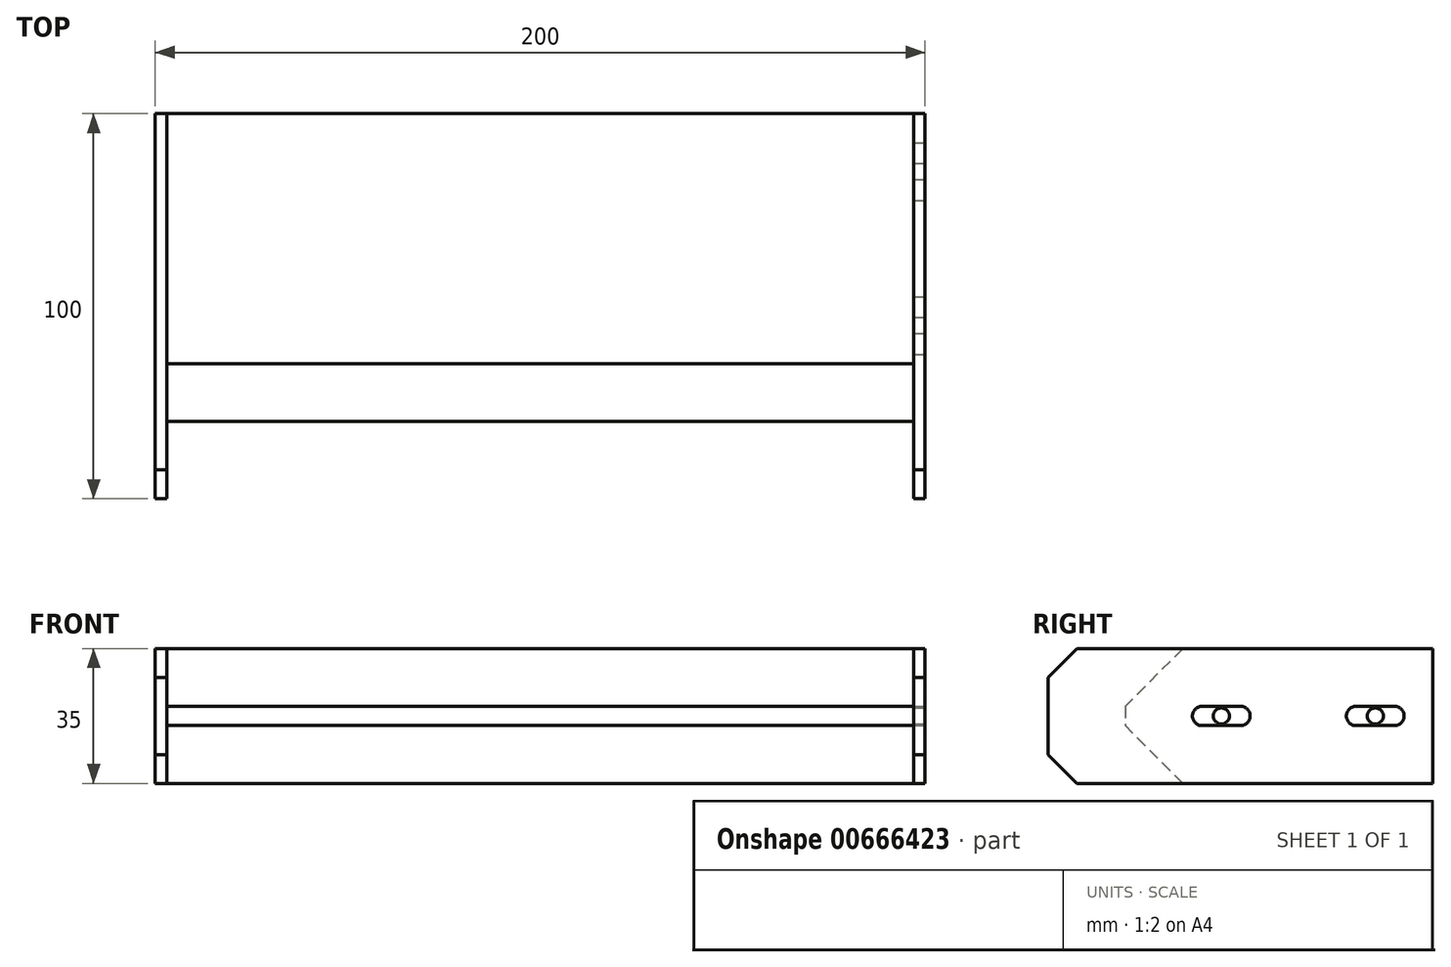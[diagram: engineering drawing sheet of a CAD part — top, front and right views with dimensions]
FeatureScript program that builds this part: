
annotation { "Feature Type Name" : "Feature", "Feature Type Description" : "" }
export const myFeature = defineFeature(function(context is Context, id is Id, definition is map)
    precondition{}
    {
        {
            var Q0;
            Q0=qCreatedBy(makeId("Top.planeOp"),FACE);
            var sketch = newSketch(context, id + "F0", { "sketchPlane" : qUnion([Q0])});
            skLineSegment(sketch, "E0.bottom", {"start": v(100, 50) * mm, "end": v(-100, 50) * mm});
            skLineSegment(sketch, "E0.top", {"start": v(100, -50) * mm, "end": v(97, -50) * mm});
            skLineSegment(sketch, "E0.left", {"start": v(100, 50) * mm, "end": v(100, -50) * mm});
            skLineSegment(sketch, "E0.right", {"start": v(-100, 50) * mm, "end": v(-100, -50) * mm});
            skPoint(sketch, "E0.middle", {"position": v(0, 0) * mm});
            skLineSegment(sketch, "E1", {"start": v(-97, -50) * mm, "end": v(-97, -30) * mm});
            skLineSegment(sketch, "E2", {"start": v(-97, -30) * mm, "end": v(97, -30) * mm});
            skLineSegment(sketch, "E3", {"start": v(97, -30) * mm, "end": v(97, -50) * mm});
            skLineSegment(sketch, "E4.trimOffspring", {"start": v(-97, -50) * mm, "end": v(-100, -50) * mm});
            skSolve(sketch);
        }
        {
            var Q0;
            Q0 = qSketchRegion(id + "F0", true);
            extrude(context, id + "F1", {"entities" : qUnion([Q0]), "depth" : 17.5 * mm, "offsetDistance" : 25 * mm, "hasSecondDirection" : true, "secondDirectionOppositeDirection" : true, "secondDirectionDepth" : 17.5 * mm});
        }
        {
            var Q0;
            Q0=makeQuery(id+"F1.opExtrude","CAP_EDGE",EDGE,{"disambiguationData":[OSD([sQuery(id+"F0.wireOp",EDGE,"E2")])],"isStart":false});
            var Q1;
            Q1=makeQuery(id+"F1.opExtrude","CAP_EDGE",EDGE,{"disambiguationData":[OSD([sQuery(id+"F0.wireOp",EDGE,"E2")])],"isStart":true});
            chamfer(context, id + "F2", {"entities" : qUnion([Q0, Q1]), "width" : 15 * mm, "tangentPropagation" : true});
        }
        {
            var Q0;
            Q0=makeQuery(id+"F1.opExtrude","CAP_EDGE",EDGE,{"disambiguationData":[OSD([sQuery(id+"F0.wireOp",EDGE,"E0.top")])],"isStart":false});
            var Q1;
            Q1=makeQuery(id+"F1.opExtrude","CAP_EDGE",EDGE,{"disambiguationData":[OSD([sQuery(id+"F0.wireOp",EDGE,"E0.top")])],"isStart":true});
            var Q2;
            Q2=makeQuery(id+"F1.opExtrude","CAP_EDGE",EDGE,{"disambiguationData":[OSD([sQuery(id+"F0.wireOp",EDGE,"E4.trimOffspring")])],"isStart":false});
            var Q3;
            Q3=makeQuery(id+"F1.opExtrude","CAP_EDGE",EDGE,{"disambiguationData":[OSD([sQuery(id+"F0.wireOp",EDGE,"E4.trimOffspring")])],"isStart":true});
            chamfer(context, id + "F3", {"entities" : qUnion([Q0, Q1, Q2, Q3]), "width" : 7.5 * mm, "tangentPropagation" : true});
        }
        {
            var Q0;
            Q0=makeQuery(id+"F1.opExtrude","SWEPT_FACE",FACE,{"disambiguationData":[OSD([sQuery(id+"F0.wireOp",EDGE,"E0.left")])]});
            var sketch = newSketch(context, id + "F4", { "sketchPlane" : qUnion([Q0])});
            skLineSegment(sketch, "E5.bottom", {"start": v(40, 2.5) * mm, "end": v(30, 2.5) * mm});
            skLineSegment(sketch, "E5.top", {"start": v(40, -2.5) * mm, "end": v(30, -2.5) * mm});
            skLineSegment(sketch, "E5.left", {"start": v(42.5, 0) * mm, "end": v(42.5, 0) * mm});
            skLineSegment(sketch, "E5.right", {"start": v(27.5, 0) * mm, "end": v(27.5, 0) * mm});
            skLineSegment(sketch, "E6.bottom", {"start": v(0, 2.5) * mm, "end": v(-10, 2.5) * mm});
            skLineSegment(sketch, "E6.top", {"start": v(0, -2.5) * mm, "end": v(-10, -2.5) * mm});
            skLineSegment(sketch, "E6.left", {"start": v(2.5, 0) * mm, "end": v(2.5, 0) * mm});
            skLineSegment(sketch, "E6.right", {"start": v(-12.5, 0) * mm, "end": v(-12.5, 0) * mm});
            skPoint(sketch, "E7.visualSharp", {"position": v(-12.5, 2.5) * mm});
            skArc(sketch, "E7.filletArc", {"start": v(-10, 2.5) * mm, "mid": v(-11.77, 1.77) * mm, "end": v(-12.5, 0) * mm});
            skPoint(sketch, "E8.visualSharp", {"position": v(-12.5, -2.5) * mm});
            skArc(sketch, "E8.filletArc", {"start": v(-12.5, 0) * mm, "mid": v(-11.77, -1.77) * mm, "end": v(-10, -2.5) * mm});
            skPoint(sketch, "E9.visualSharp", {"position": v(2.5, 2.5) * mm});
            skArc(sketch, "E9.filletArc", {"start": v(2.5, 0) * mm, "mid": v(1.77, 1.77) * mm, "end": v(0, 2.5) * mm});
            skPoint(sketch, "E10.visualSharp", {"position": v(2.5, -2.5) * mm});
            skArc(sketch, "E10.filletArc", {"start": v(0, -2.5) * mm, "mid": v(1.77, -1.77) * mm, "end": v(2.5, 0) * mm});
            skPoint(sketch, "E11.visualSharp", {"position": v(27.5, 2.5) * mm});
            skArc(sketch, "E11.filletArc", {"start": v(30, 2.5) * mm, "mid": v(28.23, 1.77) * mm, "end": v(27.5, 0) * mm});
            skPoint(sketch, "E12.visualSharp", {"position": v(27.5, -2.5) * mm});
            skArc(sketch, "E12.filletArc", {"start": v(27.5, 0) * mm, "mid": v(28.23, -1.77) * mm, "end": v(30, -2.5) * mm});
            skPoint(sketch, "E13.visualSharp", {"position": v(42.5, 2.5) * mm});
            skArc(sketch, "E13.filletArc", {"start": v(42.5, 0) * mm, "mid": v(41.77, 1.77) * mm, "end": v(40, 2.5) * mm});
            skPoint(sketch, "E14.visualSharp", {"position": v(42.5, -2.5) * mm});
            skArc(sketch, "E14.filletArc", {"start": v(40, -2.5) * mm, "mid": v(41.77, -1.77) * mm, "end": v(42.5, 0) * mm});
            skCircle(sketch, "E15", {"center": v(-5, 0) * mm, "radius": 2.1 * mm});
            skCircle(sketch, "E16", {"center": v(35, 0) * mm, "radius": 2.1 * mm});
            skPoint(sketch, "E16.centerSnap0", {"position": v(35, -2.5) * mm});
            skLineSegment(sketch, "E17", {"start": v(-50, 0) * mm, "end": v(50, 0) * mm, "construction": true});
            skSolve(sketch);
        }
        {
            var Q0;
            Q0 = qSketchRegion(id + "F4", true);
            extrude(context, id + "F5", {"entities" : qUnion([Q0]), "operationType" : NewBodyOperationType.REMOVE, "oppositeDirection" : true, "depth" : 3 * mm, "offsetDistance" : 25 * mm});
        }
        {
            var Q0;
            Q0=makeQuery(id+"F1.opExtrude","CAP_FACE",FACE,{"disambiguationData":[OSD([sQuery(id+"F0.wireOp",EDGE,"E0.bottom"),sQuery(id+"F0.wireOp",EDGE,"E0.top"),sQuery(id+"F0.wireOp",EDGE,"E0.left"),sQuery(id+"F0.wireOp",EDGE,"E0.right"),sQuery(id+"F0.wireOp",EDGE,"E1"),sQuery(id+"F0.wireOp",EDGE,"E2"),sQuery(id+"F0.wireOp",EDGE,"E3"),sQuery(id+"F0.wireOp",EDGE,"E4.trimOffspring")])],"isStart":false});
            var sketch = newSketch(context, id + "F6", { "sketchPlane" : qUnion([Q0])});
            skLineSegment(sketch, "E18.bottom", {"start": v(-100, 50) * mm, "end": v(-97, 50) * mm});
            skLineSegment(sketch, "E18.top", {"start": v(-100, -42.5) * mm, "end": v(-97, -42.5) * mm});
            skLineSegment(sketch, "E18.left", {"start": v(-100, 50) * mm, "end": v(-100, -42.5) * mm});
            skLineSegment(sketch, "E18.right", {"start": v(-97, 50) * mm, "end": v(-97, -42.5) * mm});
            skLineSegment(sketch, "E19.bottom", {"start": v(100, 50) * mm, "end": v(97, 50) * mm});
            skLineSegment(sketch, "E19.top", {"start": v(100, -42.5) * mm, "end": v(97, -42.5) * mm});
            skLineSegment(sketch, "E19.left", {"start": v(100, 50) * mm, "end": v(100, -42.5) * mm});
            skLineSegment(sketch, "E19.right", {"start": v(97, 50) * mm, "end": v(97, -42.5) * mm});
            skSolve(sketch);
        }
        {
            var Q0;
            {var subQ5=sQuery(id+"F6.wireOp",EDGE,"E19.bottom");Q0=makeQuery(id+"F6.imprint","IMPRINT",FACE,{"disambiguationData":[TD([[makeQuery(id+"F6.imprint","IMPRINT",EDGE,{"derivedFrom":subQ5}),1.0]])]});}
            var Q1;
            {var subQ4=sQuery(id+"F6.wireOp",EDGE,"E18.bottom");Q1=makeQuery(id+"F6.imprint","IMPRINT",FACE,{"disambiguationData":[TD([[makeQuery(id+"F6.imprint","IMPRINT",EDGE,{"derivedFrom":subQ4}),1.0]])]});}
            extrude(context, id + "F7", {"entities" : qUnion([Q0, Q1]), "operationType" : NewBodyOperationType.REMOVE, "oppositeDirection" : true, "depth" : 0.01 * mm, "offsetDistance" : 25 * mm});
        }
    });
